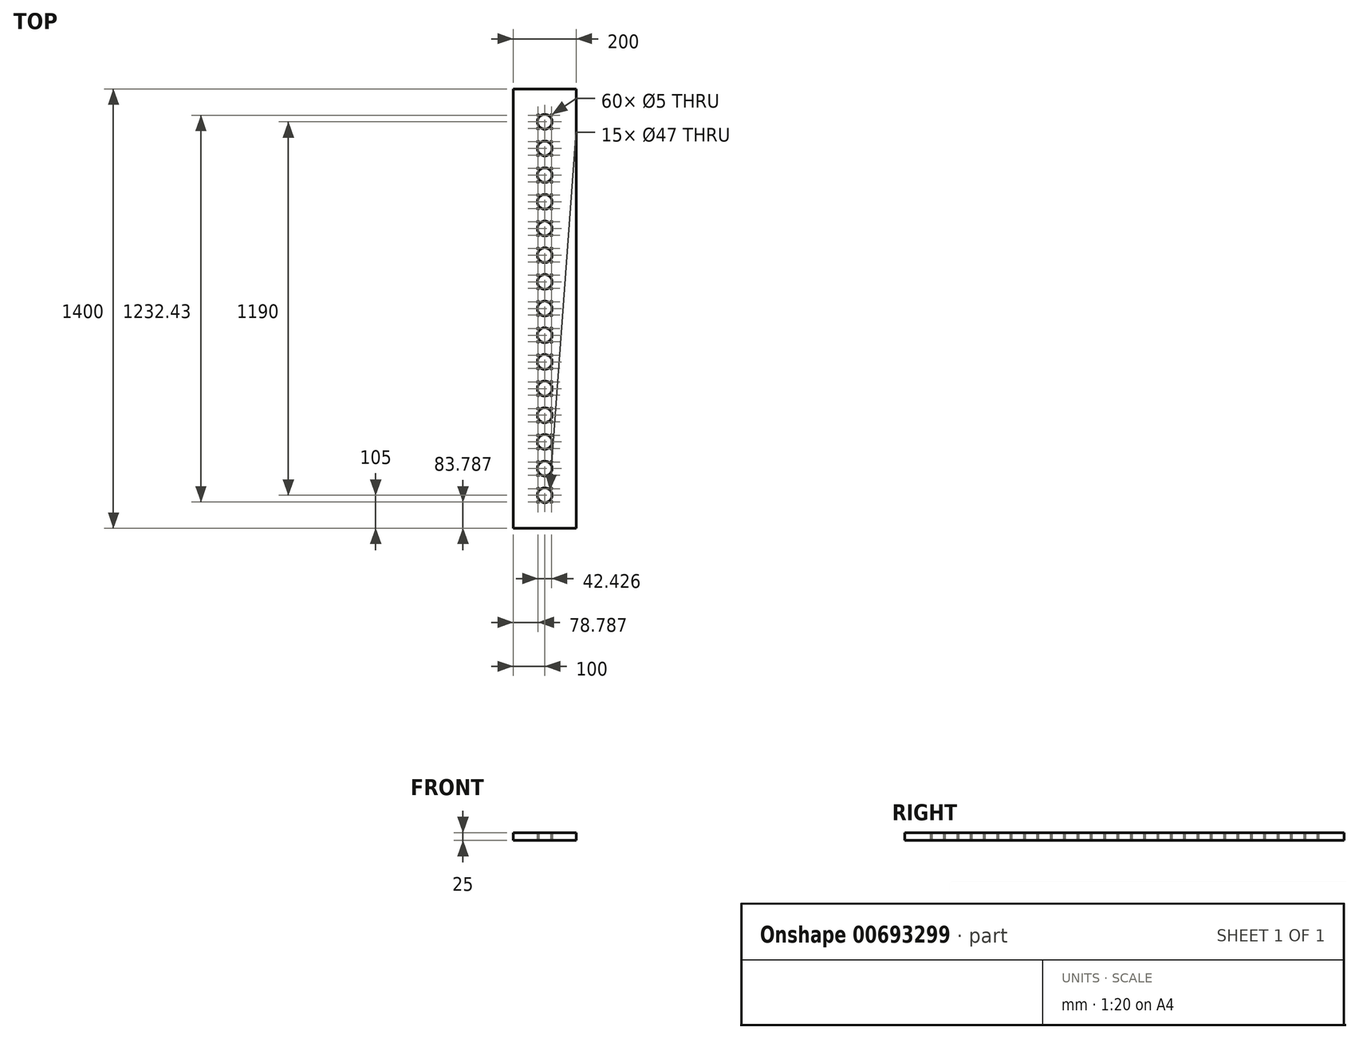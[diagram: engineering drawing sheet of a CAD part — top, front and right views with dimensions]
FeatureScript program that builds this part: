
annotation { "Feature Type Name" : "Feature", "Feature Type Description" : "" }
export const myFeature = defineFeature(function(context is Context, id is Id, definition is map)
    precondition{}
    {
        {
            var Q0;
            Q0=qCreatedBy(makeId("Top.planeOp"),FACE);
            var sketch = newSketch(context, id + "F0", { "sketchPlane" : qUnion([Q0])});
            skLineSegment(sketch, "E0.bottom", {"start": v(100, 700) * mm, "end": v(-100, 700) * mm});
            skLineSegment(sketch, "E0.top", {"start": v(100, -700) * mm, "end": v(-100, -700) * mm});
            skLineSegment(sketch, "E0.left", {"start": v(100, 700) * mm, "end": v(100, -700) * mm});
            skLineSegment(sketch, "E0.right", {"start": v(-100, 700) * mm, "end": v(-100, -700) * mm});
            skCircle(sketch, "E1", {"center": v(0, 0) * mm, "radius": 23.5 * mm});
            skCircle(sketch, "E2.0.1.0", {"center": v(0, 85) * mm, "radius": 23.5 * mm});
            skCircle(sketch, "E2.0.2.0", {"center": v(0, 170) * mm, "radius": 23.5 * mm});
            skCircle(sketch, "E2.0.3.0", {"center": v(0, 255) * mm, "radius": 23.5 * mm});
            skCircle(sketch, "E2.0.4.0", {"center": v(0, 340) * mm, "radius": 23.5 * mm});
            skCircle(sketch, "E2.0.5.0", {"center": v(0, 425) * mm, "radius": 23.5 * mm});
            skCircle(sketch, "E2.0.6.0", {"center": v(0, 510) * mm, "radius": 23.5 * mm});
            skCircle(sketch, "E2.0.7.0", {"center": v(0, 595) * mm, "radius": 23.5 * mm});
            skLineSegment(sketch, "E2.direction1", {"start": v(0, 0) * mm, "end": v(25, 0) * mm, "construction": true});
            skLineSegment(sketch, "E2.direction2", {"start": v(0, 0) * mm, "end": v(0, 85) * mm, "construction": true});
            skCircle(sketch, "E3.0.1.0", {"center": v(0, -85) * mm, "radius": 23.5 * mm});
            skCircle(sketch, "E3.0.2.0", {"center": v(0, -170) * mm, "radius": 23.5 * mm});
            skCircle(sketch, "E3.0.3.0", {"center": v(0, -255) * mm, "radius": 23.5 * mm});
            skCircle(sketch, "E3.0.4.0", {"center": v(0, -340) * mm, "radius": 23.5 * mm});
            skCircle(sketch, "E3.0.5.0", {"center": v(0, -425) * mm, "radius": 23.5 * mm});
            skCircle(sketch, "E3.0.6.0", {"center": v(0, -510) * mm, "radius": 23.5 * mm});
            skCircle(sketch, "E3.0.7.0", {"center": v(0, -595) * mm, "radius": 23.5 * mm});
            skLineSegment(sketch, "E3.direction2", {"start": v(0, 0) * mm, "end": v(0, -85) * mm, "construction": true});
            skCircle(sketch, "E4", {"center": v(-21.21, -573.79) * mm, "radius": 2.5 * mm});
            skCircle(sketch, "E5", {"center": v(0, -595) * mm, "radius": 30 * mm, "construction": true});
            skLineSegment(sketch, "E6", {"start": v(0, -595) * mm, "end": v(-30, -595) * mm, "construction": true});
            skLineSegment(sketch, "E7", {"start": v(0, -595) * mm, "end": v(0, -565) * mm, "construction": true});
            skLineSegment(sketch, "E8", {"start": v(-30, -595) * mm, "end": v(-30, -565) * mm, "construction": true});
            skLineSegment(sketch, "E9", {"start": v(-30, -565) * mm, "end": v(0, -565) * mm, "construction": true});
            skLineSegment(sketch, "E10", {"start": v(-30, -565) * mm, "end": v(0, -595) * mm, "construction": true});
            skCircle(sketch, "E11.MirrorC", {"center": v(-21.21, -616.21) * mm, "radius": 2.5 * mm});
            skCircle(sketch, "E12.MirrorC", {"center": v(21.21, -573.79) * mm, "radius": 2.5 * mm});
            skCircle(sketch, "E13.MirrorC", {"center": v(21.21, -616.21) * mm, "radius": 2.5 * mm});
            skCircle(sketch, "E14.0.1.0", {"center": v(-21.21, -531.21) * mm, "radius": 2.5 * mm});
            skCircle(sketch, "E14.0.1.1", {"center": v(21.21, -531.21) * mm, "radius": 2.5 * mm});
            skCircle(sketch, "E14.0.1.2", {"center": v(21.21, -488.79) * mm, "radius": 2.5 * mm});
            skCircle(sketch, "E14.0.1.3", {"center": v(-21.21, -488.79) * mm, "radius": 2.5 * mm});
            skCircle(sketch, "E14.0.2.0", {"center": v(-21.21, -446.21) * mm, "radius": 2.5 * mm});
            skCircle(sketch, "E14.0.2.1", {"center": v(21.21, -446.21) * mm, "radius": 2.5 * mm});
            skCircle(sketch, "E14.0.2.2", {"center": v(21.21, -403.79) * mm, "radius": 2.5 * mm});
            skCircle(sketch, "E14.0.2.3", {"center": v(-21.21, -403.79) * mm, "radius": 2.5 * mm});
            skCircle(sketch, "E14.0.3.0", {"center": v(-21.21, -361.21) * mm, "radius": 2.5 * mm});
            skCircle(sketch, "E14.0.3.1", {"center": v(21.21, -361.21) * mm, "radius": 2.5 * mm});
            skCircle(sketch, "E14.0.3.2", {"center": v(21.21, -318.79) * mm, "radius": 2.5 * mm});
            skCircle(sketch, "E14.0.3.3", {"center": v(-21.21, -318.79) * mm, "radius": 2.5 * mm});
            skCircle(sketch, "E14.0.4.0", {"center": v(-21.21, -276.21) * mm, "radius": 2.5 * mm});
            skCircle(sketch, "E14.0.4.1", {"center": v(21.21, -276.21) * mm, "radius": 2.5 * mm});
            skCircle(sketch, "E14.0.4.2", {"center": v(21.21, -233.79) * mm, "radius": 2.5 * mm});
            skCircle(sketch, "E14.0.4.3", {"center": v(-21.21, -233.79) * mm, "radius": 2.5 * mm});
            skCircle(sketch, "E14.0.5.0", {"center": v(-21.21, -191.21) * mm, "radius": 2.5 * mm});
            skCircle(sketch, "E14.0.5.1", {"center": v(21.21, -191.21) * mm, "radius": 2.5 * mm});
            skCircle(sketch, "E14.0.5.2", {"center": v(21.21, -148.79) * mm, "radius": 2.5 * mm});
            skCircle(sketch, "E14.0.5.3", {"center": v(-21.21, -148.79) * mm, "radius": 2.5 * mm});
            skCircle(sketch, "E14.0.6.0", {"center": v(-21.21, -106.21) * mm, "radius": 2.5 * mm});
            skCircle(sketch, "E14.0.6.1", {"center": v(21.21, -106.21) * mm, "radius": 2.5 * mm});
            skCircle(sketch, "E14.0.6.2", {"center": v(21.21, -63.79) * mm, "radius": 2.5 * mm});
            skCircle(sketch, "E14.0.6.3", {"center": v(-21.21, -63.79) * mm, "radius": 2.5 * mm});
            skCircle(sketch, "E14.0.7.0", {"center": v(-21.21, -21.21) * mm, "radius": 2.5 * mm});
            skCircle(sketch, "E14.0.7.1", {"center": v(21.21, -21.21) * mm, "radius": 2.5 * mm});
            skCircle(sketch, "E14.0.7.2", {"center": v(21.21, 21.21) * mm, "radius": 2.5 * mm});
            skCircle(sketch, "E14.0.7.3", {"center": v(-21.21, 21.21) * mm, "radius": 2.5 * mm});
            skCircle(sketch, "E14.0.8.0", {"center": v(-21.21, 63.79) * mm, "radius": 2.5 * mm});
            skCircle(sketch, "E14.0.8.1", {"center": v(21.21, 63.79) * mm, "radius": 2.5 * mm});
            skCircle(sketch, "E14.0.8.2", {"center": v(21.21, 106.21) * mm, "radius": 2.5 * mm});
            skCircle(sketch, "E14.0.8.3", {"center": v(-21.21, 106.21) * mm, "radius": 2.5 * mm});
            skCircle(sketch, "E14.0.9.0", {"center": v(-21.21, 148.79) * mm, "radius": 2.5 * mm});
            skCircle(sketch, "E14.0.9.1", {"center": v(21.21, 148.79) * mm, "radius": 2.5 * mm});
            skCircle(sketch, "E14.0.9.2", {"center": v(21.21, 191.21) * mm, "radius": 2.5 * mm});
            skCircle(sketch, "E14.0.9.3", {"center": v(-21.21, 191.21) * mm, "radius": 2.5 * mm});
            skCircle(sketch, "E14.0.10.0", {"center": v(-21.21, 233.79) * mm, "radius": 2.5 * mm});
            skCircle(sketch, "E14.0.10.1", {"center": v(21.21, 233.79) * mm, "radius": 2.5 * mm});
            skCircle(sketch, "E14.0.10.2", {"center": v(21.21, 276.21) * mm, "radius": 2.5 * mm});
            skCircle(sketch, "E14.0.10.3", {"center": v(-21.21, 276.21) * mm, "radius": 2.5 * mm});
            skCircle(sketch, "E14.0.11.0", {"center": v(-21.21, 318.79) * mm, "radius": 2.5 * mm});
            skCircle(sketch, "E14.0.11.1", {"center": v(21.21, 318.79) * mm, "radius": 2.5 * mm});
            skCircle(sketch, "E14.0.11.2", {"center": v(21.21, 361.21) * mm, "radius": 2.5 * mm});
            skCircle(sketch, "E14.0.11.3", {"center": v(-21.21, 361.21) * mm, "radius": 2.5 * mm});
            skCircle(sketch, "E14.0.12.0", {"center": v(-21.21, 403.79) * mm, "radius": 2.5 * mm});
            skCircle(sketch, "E14.0.12.1", {"center": v(21.21, 403.79) * mm, "radius": 2.5 * mm});
            skCircle(sketch, "E14.0.12.2", {"center": v(21.21, 446.21) * mm, "radius": 2.5 * mm});
            skCircle(sketch, "E14.0.12.3", {"center": v(-21.21, 446.21) * mm, "radius": 2.5 * mm});
            skCircle(sketch, "E14.0.13.0", {"center": v(-21.21, 488.79) * mm, "radius": 2.5 * mm});
            skCircle(sketch, "E14.0.13.1", {"center": v(21.21, 488.79) * mm, "radius": 2.5 * mm});
            skCircle(sketch, "E14.0.13.2", {"center": v(21.21, 531.21) * mm, "radius": 2.5 * mm});
            skCircle(sketch, "E14.0.13.3", {"center": v(-21.21, 531.21) * mm, "radius": 2.5 * mm});
            skCircle(sketch, "E14.0.14.0", {"center": v(-21.21, 573.79) * mm, "radius": 2.5 * mm});
            skCircle(sketch, "E14.0.14.1", {"center": v(21.21, 573.79) * mm, "radius": 2.5 * mm});
            skCircle(sketch, "E14.0.14.2", {"center": v(21.21, 616.21) * mm, "radius": 2.5 * mm});
            skCircle(sketch, "E14.0.14.3", {"center": v(-21.21, 616.21) * mm, "radius": 2.5 * mm});
            skLineSegment(sketch, "E14.direction1", {"start": v(-21.21, -616.21) * mm, "end": v(3.79, -616.21) * mm, "construction": true});
            skLineSegment(sketch, "E14.direction2", {"start": v(-21.21, -616.21) * mm, "end": v(-21.21, -531.21) * mm, "construction": true});
            skSolve(sketch);
        }
        {
            var Q0;
            Q0 = qSketchRegion(id + "F0", true);
            extrude(context, id + "F1", {"entities" : qUnion([Q0]), "depth" : 25 * mm, "offsetDistance" : 25 * mm});
        }
    });
